# Revit family: TOMACORRIENTES DOBLE
name_source: partatom
category: Electrical Fixtures
units: mm (PartAtom-declared; Revit-internal decimal feet)

## family parameters
Always vertical = No
Cut with Voids When Loaded = No
Maintain Annotation Orientation = No
Part Type = Normal
Room Calculation Point = No
Round Connector Dimension = Use Diameter
Shared = Yes
Work Plane-Based = Yes

## types (1)
- TOMACORRIENTES DOBLE
    A1 = 32 mm
    A2 = 8 mm  [stored 0.0262467 ft]
    A3 = 2 mm  [stored 0.00656168 ft]
    ANCHO BASE = 45 mm  [stored 0.147638 ft]
    ANCHO CONECTOR = 29 mm  [stored 0.0951444 ft]
    ANCHO RANURA = 2 mm  [stored 0.00656168 ft]
    ANCHO RECEPTACULO = 36 mm  [stored 0.11811 ft]
    ANCHO TIERRA = 5 mm  [stored 0.0164042 ft]
    Default Elevation = 1219 mm
    E1 = 3 mm  [stored 0.00984252 ft]
    ESPESOR = 8 mm  [stored 0.0262467 ft]
    ESPESOR BASE = 3 mm  [stored 0.00984252 ft]
    ESPESOR CONECTOR = 10 mm  [stored 0.0328084 ft]
    INCLUIR EN LISTADO = No
    LARGO BASE = 69 mm  [stored 0.226378 ft]
    LARGO CONECTOR = 63 mm
    LARGO NEGATIVO = 7 mm  [stored 0.0229659 ft]
    LARGO POSITIVO = 9 mm  [stored 0.0295276 ft]
    LARGO TIERRA = 3 mm  [stored 0.00984252 ft]
    LONGITUD RECEPTACULO = 65 mm  [stored 0.213255 ft]
    RADIO_1 = 1 mm  [stored 0.00328084 ft]
    SEP = 15 mm  [stored 0.0492126 ft]
    SEP BORDE = 4 mm  [stored 0.0131234 ft]
    SEP RANURAS = 11 mm  [stored 0.0360892 ft]
    SEP TIERRAS = 39 mm  [stored 0.127953 ft]
    X1 = 4 mm  [stored 0.0131234 ft]
    X2 = 11 mm  [stored 0.0360892 ft]
    X3 = 25 mm  [stored 0.082021 ft]
    X4 = 2 mm  [stored 0.00656168 ft]
    Y = 2 mm  [stored 0.00656168 ft]

note: [stored X ft] marks values corroborated as IEEE doubles in the binary element streams (Revit-internal decimal feet)

## geometry (parser evidence)
native form markers: Sweep x6
no freeform markers — native parametric forms only
